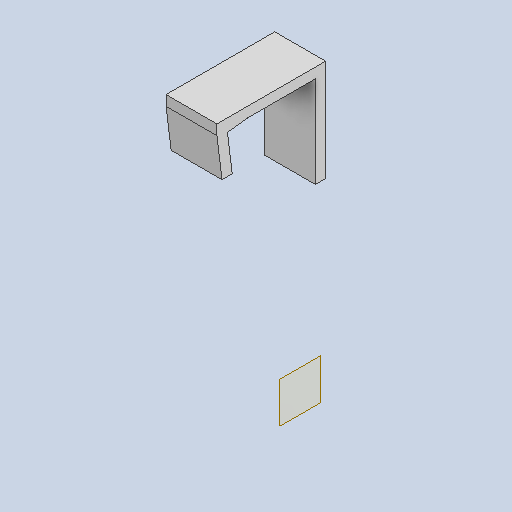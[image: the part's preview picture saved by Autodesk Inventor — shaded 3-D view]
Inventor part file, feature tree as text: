
AUTODESK INVENTOR PART (.ipt)
format: ipt  version: 2023 (Build 270158000, 158)  size: 105,472 bytes
history: native  units: mm
features: other x3, extrude x2, reference x2, plane x1, sketch x1
ambient origin geometry x8: Origin, YZ Plane, XZ Plane, XY Plane, X Axis, Y Axis, Z Axis, Center Point
bodies: Solid1 (feature_tree)
feature tree (9):
  plane  "Work Plane1"
  sketch  "Sketch2"  dims[d0=78.575mm d2=5.0mm d3=20.0mm d4=50.0mm d5=5.0mm d6=5.0mm d7=40.0mm d8=5.0mm d9=0.95mm d10=25.0mm d11=0.0mm d12=13.2mm d13=0.0mm]
  extrude  "Extrusion1"  Depth=5.0mm
  extrude  "Extrusion2"  Depth=20.0mm
  reference  "Reference1"
  reference  "Reference2"
  other  "Assembly1"
  other  "Album:1"
  other  "wall:1"
